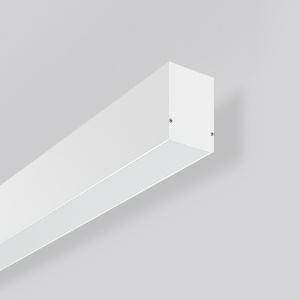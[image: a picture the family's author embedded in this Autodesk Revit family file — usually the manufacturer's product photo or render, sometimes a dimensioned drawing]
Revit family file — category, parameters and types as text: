
# Revit family: less_is_more_50_312605_002_1_bfb3
name_source: partatom
category: Lighting Fixtures
units: mm (PartAtom-declared; Revit-internal decimal feet)

## family parameters
Cut with Voids When Loaded = No
Host = Face
Light Source = No
Part Type = Normal
Room Calculation Point = No
Round Connector Dimension = Use Diameter
Shared = No

## types (1)
- LESS IS MORE 50 (1 x LED Modul 840, 1150 lm, 4000)
    Apparent Load = 9 VA
    CIE Flux Codes = 48 80 96 100 100
    Color Rendering = 80
    Color Temperature = 4000
    Default Elevation = 1800 mm
    Description = Series: LESS IS MORE 50
Linear wall luminaires. Housing: extruded aluminium profile, powder-coated. End cap aluminium powder-coated. Diffuser made of non-yellowing plastic (PMMA), opal. Direct light emission. Suitable for Wall (surface). LED unit with integrated converter interchangeable and removable. Suitable for through-wiring. With sensors or as a safety luminaire on request. 
Colour: traffic white, matt (RAL 9016)
Length: 847 mm
Width: 67 mm
Height: 75 mm
Lamp: LED
Socket: without socket
Colour temperature: 4000K
Colour rendering index (CRI): 80
System power: 9 W
Rated luminous flux: 1150 lm
Luminous efficiency: 128 lm/W
Control gear: Regulated power supply
Protection class: I
Type of protection: IP 20
    Height = 75 mm
    Lamp = 1 x LED Modul 840
    Lamp Light Flux = 1150 lm
    Lamp count = 1
    Length = 847 mm
    Lifetime = 50000 h
    Luminous efficacy = 128 lm/W
    Manufacturer = RZB
    ModVariant = No
    Model = 312605.002.1
    Mounting Place = Wall
    Mounting Type = Surface mounted
    Number of Poles = 1
    OnlyDefault = Yes
    Power Factor = 1
    Product Name = LESS IS MORE 50
    Product group = Surface mounted LED linear luminaires
    ProductGroupID = 2007
    Protection Class = Protection class I
    Protection Degree = IP 20
    RLX_Detail_Level = 1
    RLX_Emergency_Light_Flux = 0 lm
    RLX_Emergency_Type = 0
    RLX_Emergency_Type_DB = No
    RlxData = <blob elided: 35113 chars, md5=d41a8a3b>
    Socket = socket
    Standby Power = 0 W
    System Light Flux = 1150 lm
    System Power = 9 W
    Type Comments = Product without accessories
    Type Image = 312606.002.jpg
    URL = http://relux.com
    VarID = ---
    Voltage = 0 V
    Weight = 0.00 kg
    Width = 67 mm

## geometry (parser evidence)
native form markers: Blend x4, Sweep x11
no freeform markers — native parametric forms only
